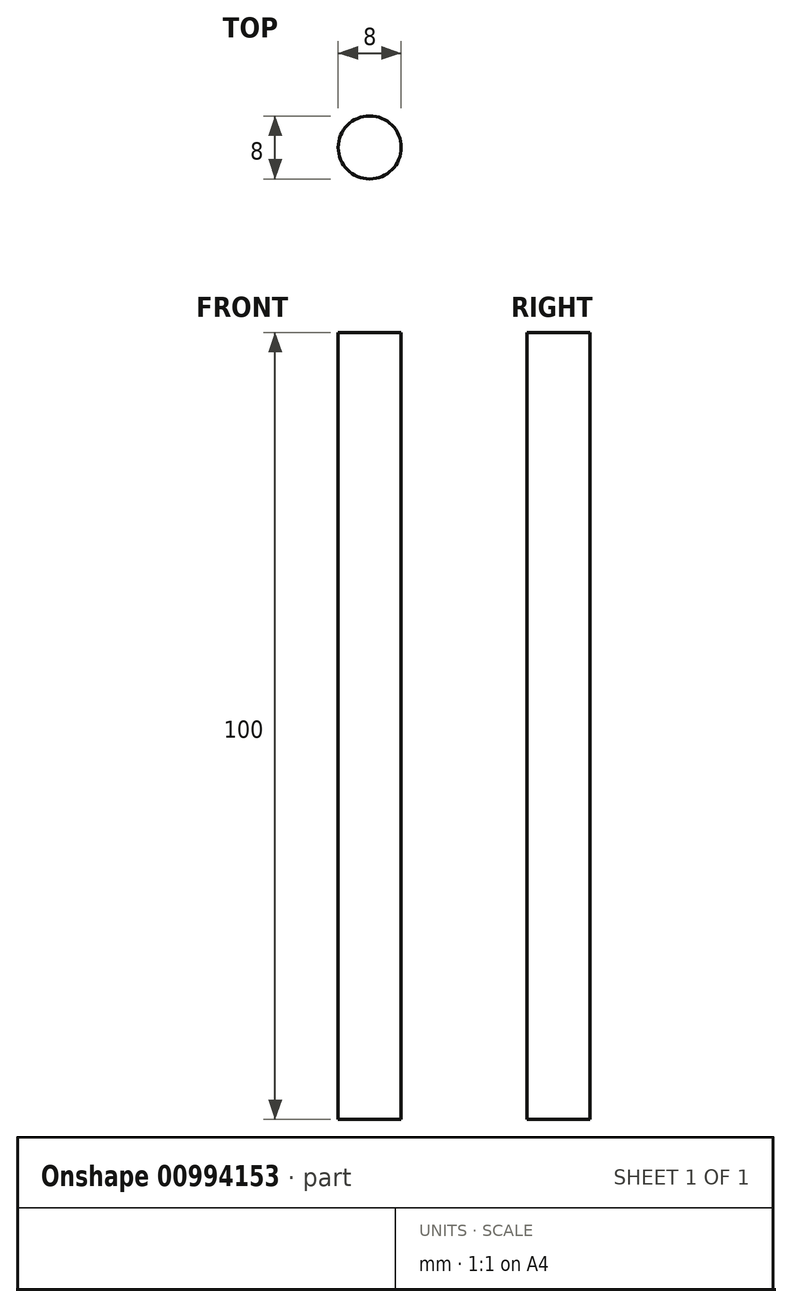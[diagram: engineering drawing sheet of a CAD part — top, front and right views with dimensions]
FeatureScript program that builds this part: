
annotation { "Feature Type Name" : "Feature", "Feature Type Description" : "" }
export const myFeature = defineFeature(function(context is Context, id is Id, definition is map)
    precondition{}
    {
        {
            var Q0;
            Q0=qCreatedBy(makeId("Top.planeOp"),FACE);
            var sketch = newSketch(context, id + "F0", { "sketchPlane" : qUnion([Q0])});
            skCircle(sketch, "E0", {"center": v(0, 0) * mm, "radius": 4 * mm});
            skSolve(sketch);
        }
        {
            var Q0;
            Q0 = qSketchRegion(id + "F0", true);
            extrude(context, id + "F1", {"entities" : qUnion([Q0]), "depth" : 100 * mm, "offsetDistance" : 25 * mm});
        }
    });
